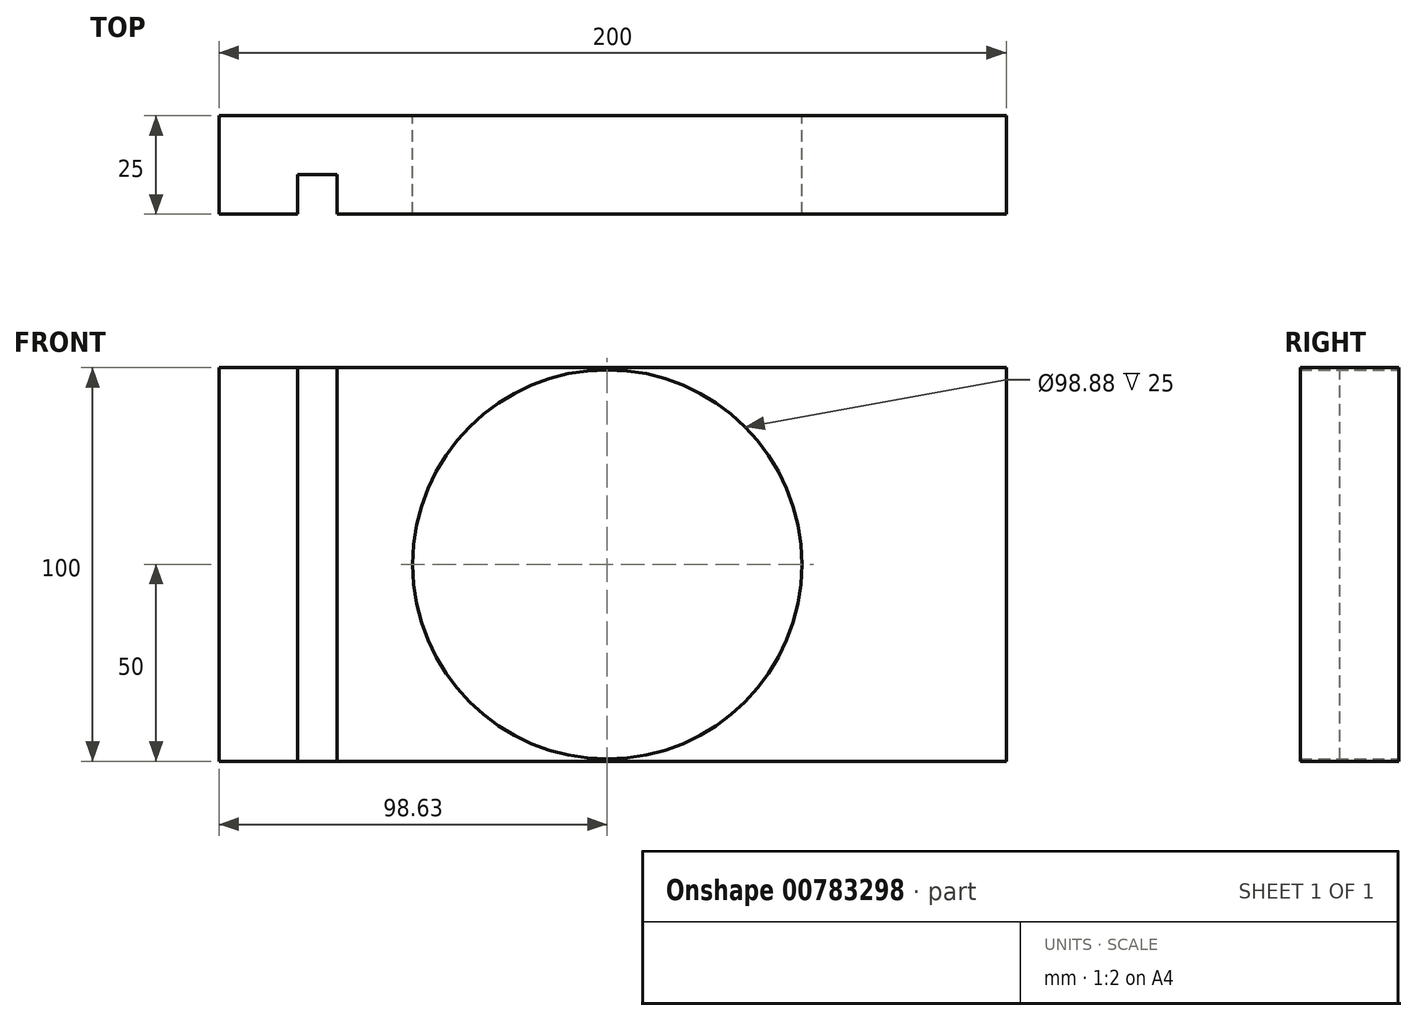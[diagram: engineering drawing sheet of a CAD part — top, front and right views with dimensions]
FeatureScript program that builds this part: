
annotation { "Feature Type Name" : "Feature", "Feature Type Description" : "" }
export const myFeature = defineFeature(function(context is Context, id is Id, definition is map)
    precondition{}
    {
        {
            var Q0;
            Q0=qCreatedBy(makeId("Front.planeOp"),FACE);
            var sketch = newSketch(context, id + "F0", { "sketchPlane" : qUnion([Q0])});
            skLineSegment(sketch, "E0.bottom", {"start": v(101.37, -50) * mm, "end": v(-98.63, -50) * mm});
            skLineSegment(sketch, "E0.top", {"start": v(101.37, 50) * mm, "end": v(-98.63, 50) * mm});
            skLineSegment(sketch, "E0.left", {"start": v(101.37, -50) * mm, "end": v(101.37, 50) * mm});
            skLineSegment(sketch, "E0.right", {"start": v(-98.63, -50) * mm, "end": v(-98.63, 50) * mm});
            skPoint(sketch, "E0.middle", {"position": v(1.37, 0) * mm});
            skCircle(sketch, "E1", {"center": v(0, 0) * mm, "radius": 49.44 * mm});
            skSolve(sketch);
        }
        {
            var Q0;
            Q0=makeQuery(id+"F0.imprint","IMPRINT",FACE,{"disambiguationData":[TD([[makeQuery(id+"F0.imprint","IMPRINT",EDGE,{"derivedFrom":sQuery(id+"F0.wireOp",EDGE,"E0.bottom")}),-1.0]])]});
            extrude(context, id + "F1", {"entities" : qUnion([Q0]), "depth" : 25 * mm, "offsetDistance" : 25 * mm});
        }
        {
            var Q0;
            Q0=makeQuery(id+"F1.opExtrude","CAP_FACE",FACE,{"disambiguationData":[OSD([sQuery(id+"F0.wireOp",EDGE,"E0.bottom"),sQuery(id+"F0.wireOp",EDGE,"E0.top"),sQuery(id+"F0.wireOp",EDGE,"E0.left"),sQuery(id+"F0.wireOp",EDGE,"E0.right"),sQuery(id+"F0.wireOp",EDGE,"E1")])],"isStart":false});
            var sketch = newSketch(context, id + "F2", { "sketchPlane" : qUnion([Q0])});
            skLineSegment(sketch, "E2.bottom", {"start": v(-78.63, 50) * mm, "end": v(-68.63, 50) * mm});
            skLineSegment(sketch, "E2.top", {"start": v(-78.63, -50) * mm, "end": v(-68.63, -50) * mm});
            skLineSegment(sketch, "E2.left", {"start": v(-68.63, 50) * mm, "end": v(-68.63, -50) * mm});
            skLineSegment(sketch, "E2.right", {"start": v(-78.63, 50) * mm, "end": v(-78.63, -50) * mm});
            skSolve(sketch);
        }
        {
            var Q0;
            Q0=makeQuery(id+"F2.imprint","IMPRINT",FACE,{"disambiguationData":[TD([[makeQuery(id+"F2.imprint","IMPRINT",EDGE,{"derivedFrom":sQuery(id+"F2.wireOp",EDGE,"E2.bottom")}),1.0]])]});
            extrude(context, id + "F3", {"entities" : qUnion([Q0]), "operationType" : NewBodyOperationType.REMOVE, "oppositeDirection" : true, "depth" : 10 * mm, "offsetDistance" : 25 * mm});
        }
    });
